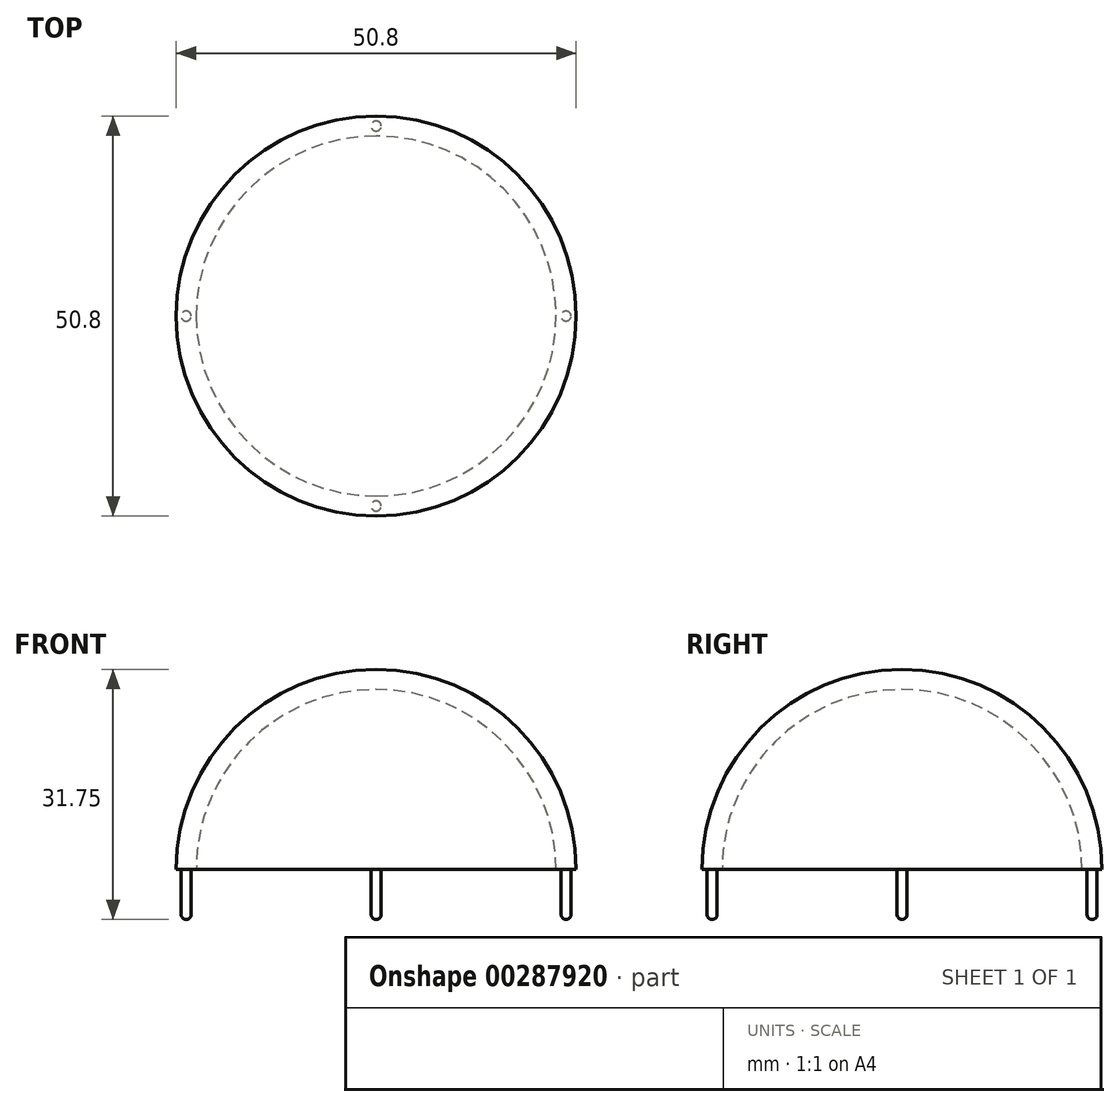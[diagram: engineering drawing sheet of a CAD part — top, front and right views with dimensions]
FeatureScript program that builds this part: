
annotation { "Feature Type Name" : "Feature", "Feature Type Description" : "" }
export const myFeature = defineFeature(function(context is Context, id is Id, definition is map)
    precondition{}
    {
        {
            var Q0;
            Q0=qCreatedBy(makeId("Top.planeOp"),FACE);
            var sketch = newSketch(context, id + "F0", { "sketchPlane" : qUnion([Q0])});
            skCircle(sketch, "E0", {"center": v(0, 0) * mm, "radius": 25.4 * mm});
            skLineSegment(sketch, "E1", {"start": v(0, 25.4) * mm, "end": v(0, -25.4) * mm});
            skSolve(sketch);
        }
        {
            var Q0;
            {var subQ0=sQuery(id+"F0.wireOp",EDGE,"E1");Q0=makeQuery(id+"F0.imprint","IMPRINT",FACE,{"disambiguationData":[TD([[makeQuery(id+"F0.imprint","IMPRINT",EDGE,{"derivedFrom":subQ0}),1.0]])]});}
            var Q1;
            Q1=sQuery(id+"F0.wireOp",EDGE,"E1");
            revolve(context, id + "F1", {"surfaceOperationType" : NewSurfaceOperationType.NEW, "entities" : qUnion([Q0]), "axis" : qUnion([Q1]), "revolveType" : RevolveType.ONE_DIRECTION, "angle" : 180 * degree});
        }
        {
            var Q0;
            Q0=makeQuery(id+"F1.opRevolve","CAP_FACE",FACE,{"disambiguationData":[OSD([sQuery(id+"F0.wireOp",EDGE,"E0"),sQuery(id+"F0.wireOp",EDGE,"E1")])],"isStart":true});
            shell(context, id + "F2", {"entities" : qUnion([Q0]), "thickness" : 2.54 * mm});
        }
        {
            var Q0;
            Q0=makeQuery(id+"F1.opRevolve","CAP_FACE",FACE,{"disambiguationData":[OSD([sQuery(id+"F0.wireOp",EDGE,"E0"),sQuery(id+"F0.wireOp",EDGE,"E1")])],"isStart":true});
            var sketch = newSketch(context, id + "F3", { "sketchPlane" : qUnion([Q0])});
            skLineSegment(sketch, "E2", {"start": v(22.86, 0) * mm, "end": v(-22.86, 0) * mm});
            skLineSegment(sketch, "E3", {"start": v(-22.86, 0) * mm, "end": v(-24.14, 0) * mm});
            skLineSegment(sketch, "E4", {"start": v(22.86, 0) * mm, "end": v(24.12, 0) * mm});
            skPoint(sketch, "E5", {"position": v(24.12, 0) * mm});
            skPoint(sketch, "E6", {"position": v(-24.14, 0) * mm});
            skLineSegment(sketch, "E7", {"start": v(0, 22.86) * mm, "end": v(0, -22.86) * mm});
            skLineSegment(sketch, "E8", {"start": v(0, 22.86) * mm, "end": v(0, 24.13) * mm});
            skLineSegment(sketch, "E9", {"start": v(0, -22.86) * mm, "end": v(0, -24.14) * mm});
            skPoint(sketch, "E10", {"position": v(0, -24.14) * mm});
            skPoint(sketch, "E11", {"position": v(0, 24.13) * mm});
            skCircle(sketch, "E12", {"center": v(0, 24.13) * mm, "radius": 0.64 * mm});
            skCircle(sketch, "E13", {"center": v(24.12, 0) * mm, "radius": 0.63 * mm});
            skCircle(sketch, "E14", {"center": v(0, -24.14) * mm, "radius": 0.64 * mm});
            skCircle(sketch, "E15", {"center": v(-24.14, 0) * mm, "radius": 0.64 * mm});
            skSolve(sketch);
        }
        {
            var Q0;
            Q0 = qSketchRegion(id + "F3", true);
            extrude(context, id + "F4", {"entities" : qUnion([Q0]), "operationType" : NewBodyOperationType.ADD, "depth" : 6.35 * mm, "offsetDistance" : 25.4 * mm});
        }
        {
            var Q0;
            Q0=makeQuery(id+"F4.opExtrude","CAP_EDGE",EDGE,{"disambiguationData":[OSD([sQuery(id+"F3.wireOp",EDGE,"E13")])],"isStart":false});
            var Q1;
            Q1=makeQuery(id+"F4.opExtrude","CAP_EDGE",EDGE,{"disambiguationData":[OSD([sQuery(id+"F3.wireOp",EDGE,"E12")])],"isStart":false});
            var Q2;
            Q2=makeQuery(id+"F4.opExtrude","CAP_EDGE",EDGE,{"disambiguationData":[OSD([sQuery(id+"F3.wireOp",EDGE,"E15")])],"isStart":false});
            var Q3;
            Q3=makeQuery(id+"F4.opExtrude","CAP_EDGE",EDGE,{"disambiguationData":[OSD([sQuery(id+"F3.wireOp",EDGE,"E14")])],"isStart":false});
            fillet(context, id + "F5", {"entities" : qUnion([Q0, Q1, Q2, Q3]), "radius" : 0.62 * mm, "tangentPropagation" : true, "allowEdgeOverflow" : false});
        }
    });
